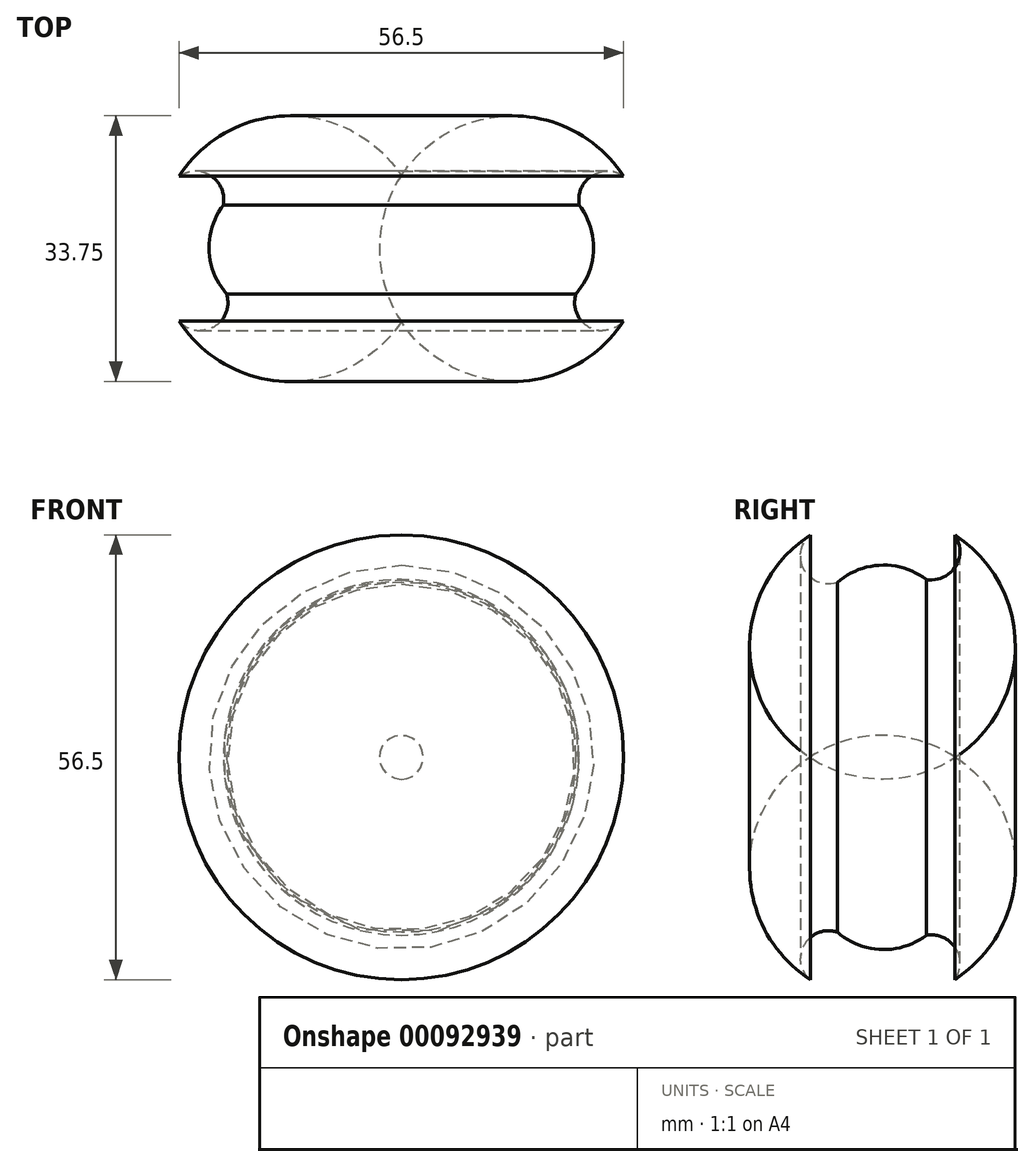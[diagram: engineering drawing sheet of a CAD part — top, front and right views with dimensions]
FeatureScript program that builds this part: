
annotation { "Feature Type Name" : "Feature", "Feature Type Description" : "" }
export const myFeature = defineFeature(function(context is Context, id is Id, definition is map)
    precondition{}
    {
        {
            var Q0;
            Q0=qCreatedBy(makeId("Top.planeOp"),FACE);
            var sketch = newSketch(context, id + "F0", { "sketchPlane" : qUnion([Q0])});
            skArc(sketch, "E0", {"start": v(22.2, -8.17) * mm, "mid": v(24.42, -2.6) * mm, "end": v(22.6, 3.13) * mm});
            skArc(sketch, "E1", {"start": v(28.25, -11.6) * mm, "mid": v(30.97, -2.42) * mm, "end": v(28.25, 6.76) * mm});
            skArc(sketch, "E2", {"start": v(28.25, 6.76) * mm, "mid": v(24.21, 6.83) * mm, "end": v(22.6, 3.13) * mm});
            skArc(sketch, "E3", {"start": v(22.2, -8.17) * mm, "mid": v(23.82, -12.37) * mm, "end": v(28.25, -11.6) * mm});
            skLineSegment(sketch, "E4", {"start": v(0, 12.2) * mm, "end": v(0, -15.03) * mm});
            skSolve(sketch);
        }
        {
            var Q0;
            Q0=makeQuery(id+"F0.imprint","IMPRINT",FACE,{"disambiguationData":[TD([[makeQuery(id+"F0.imprint","IMPRINT",EDGE,{"derivedFrom":sQuery(id+"F0.wireOp",EDGE,"E0")}),-1.0]])]});
            var Q1;
            Q1=sQuery(id+"F0.wireOp",EDGE,"E4");
            revolve(context, id + "F1", {"entities" : qUnion([Q0]), "axis" : qUnion([Q1]), "revolveType" : RevolveType.FULL});
        }
        {
            var Q0;
            Q0=qCreatedBy(makeId("Top.planeOp"),FACE);
            cPlane(context, id + "F2", {"entities" : qUnion([Q0]), "cplaneType" : CPlaneType.OFFSET, "offset" : 29 * mm, "width" : 152.4 * mm, "height" : 152.4 * mm});
        }
        {
            var Q0;
            Q0=qCreatedBy(id+"F2.planeOp",FACE);
            var sketch = newSketch(context, id + "F3", { "sketchPlane" : qUnion([Q0])});
            skCircle(sketch, "E5", {"center": v(0, -2.72) * mm, "radius": 23.46 * mm});
            skSolve(sketch);
        }
        {
            var Q0;
            Q0 = qSketchRegion(id + "F3", true);
            extrude(context, id + "F4", {"entities" : qUnion([Q0]), "operationType" : NewBodyOperationType.ADD, "depth" : 7 * mm});
        }
        {
            var Q0;
            Q0=makeQuery(id+"F4.opExtrude","CAP_FACE",FACE,{"disambiguationData":[OSD([sQuery(id+"F3.wireOp",EDGE,"E5")])],"isStart":false});
            var sketch = newSketch(context, id + "F5", { "sketchPlane" : qUnion([Q0])});
            skCircle(sketch, "E6", {"center": v(0, -2.72) * mm, "radius": 21.3 * mm});
            skSolve(sketch);
        }
        {
            var Q0;
            Q0 = qSketchRegion(id + "F5", true);
            extrude(context, id + "F6", {"entities" : qUnion([Q0]), "operationType" : NewBodyOperationType.REMOVE, "oppositeDirection" : true, "depth" : 2 * mm});
        }
        {
            var Q0;
            Q0=makeQuery(id+"F6.boolean.opBoolean","COPY",FACE,{"derivedFrom":makeQuery(id+"F6.opExtrude","CAP_FACE",FACE,{"disambiguationData":[OSD([sQuery(id+"F5.wireOp",EDGE,"E6")])],"isStart":false})});
            var sketch = newSketch(context, id + "F7", { "sketchPlane" : qUnion([Q0])});
            skLineSegment(sketch, "E7.bottom", {"start": v(-11.46, 11.21) * mm, "end": v(11.54, 11.21) * mm});
            skLineSegment(sketch, "E7.top", {"start": v(-11.46, 6.21) * mm, "end": v(-6.41, 6.21) * mm});
            skLineSegment(sketch, "E7.left", {"start": v(-11.46, 11.21) * mm, "end": v(-11.46, 6.21) * mm});
            skLineSegment(sketch, "E7.right", {"start": v(11.54, 11.21) * mm, "end": v(11.54, 6.21) * mm});
            skArc(sketch, "E8", {"start": v(-6.41, 6.21) * mm, "mid": v(-11, -2.84) * mm, "end": v(-6.22, -11.8) * mm});
            skLineSegment(sketch, "E9.bottom", {"start": v(11.54, -11.8) * mm, "end": v(6.22, -11.8) * mm});
            skLineSegment(sketch, "E9.top", {"start": v(11.54, -16.8) * mm, "end": v(-11.46, -16.8) * mm});
            skLineSegment(sketch, "E9.left", {"start": v(11.54, -11.8) * mm, "end": v(11.54, -16.8) * mm});
            skLineSegment(sketch, "E9.right", {"start": v(-11.46, -11.8) * mm, "end": v(-11.46, -16.8) * mm});
            skLineSegment(sketch, "E10.trimOffspring", {"start": v(6.41, 6.21) * mm, "end": v(11.54, 6.21) * mm});
            skLineSegment(sketch, "E11.trimOffspring", {"start": v(-6.22, -11.8) * mm, "end": v(-11.46, -11.8) * mm});
            skArc(sketch, "E12.trimOffspring", {"start": v(6.22, -11.8) * mm, "mid": v(11, -2.84) * mm, "end": v(6.41, 6.21) * mm});
            skSolve(sketch);
        }
        {
            var Q0;
            Q0 = qSketchRegion(id + "F7", true);
            extrude(context, id + "F8", {"entities" : qUnion([Q0]), "operationType" : NewBodyOperationType.ADD, "depth" : 3.5 * mm});
        }
        {
            var Q0;
            Q0=makeQuery(id+"F8.opExtrude","CAP_FACE",FACE,{"disambiguationData":[OSD([sQuery(id+"F7.wireOp",EDGE,"E7.bottom"),sQuery(id+"F7.wireOp",EDGE,"E7.top"),sQuery(id+"F7.wireOp",EDGE,"E7.left"),sQuery(id+"F7.wireOp",EDGE,"E7.right"),sQuery(id+"F7.wireOp",EDGE,"E8"),sQuery(id+"F7.wireOp",EDGE,"E9.bottom"),sQuery(id+"F7.wireOp",EDGE,"E9.top"),sQuery(id+"F7.wireOp",EDGE,"E9.left"),sQuery(id+"F7.wireOp",EDGE,"E9.right"),sQuery(id+"F7.wireOp",EDGE,"E10.trimOffspring"),sQuery(id+"F7.wireOp",EDGE,"E11.trimOffspring"),sQuery(id+"F7.wireOp",EDGE,"E12.trimOffspring")])],"isStart":false});
            var sketch = newSketch(context, id + "F9", { "sketchPlane" : qUnion([Q0])});
            skCircle(sketch, "E13", {"center": v(0, -2.72) * mm, "radius": 8.07 * mm});
            skSolve(sketch);
        }
        {
            var Q0;
            Q0 = qSketchRegion(id + "F9", true);
            extrude(context, id + "F10", {"entities" : qUnion([Q0]), "operationType" : NewBodyOperationType.REMOVE, "oppositeDirection" : true, "depth" : 2 * mm});
        }
        {
            var Q0;
            Q0=makeQuery(id+"F4.opExtrude","CAP_EDGE",EDGE,{"disambiguationData":[OSD([sQuery(id+"F3.wireOp",EDGE,"E5")])],"isStart":true});
            var Q1;
            Q1=makeQuery(id+"F4.opExtrude","CAP_EDGE",EDGE,{"disambiguationData":[OSD([sQuery(id+"F3.wireOp",EDGE,"E5")])],"isStart":false});
            fillet(context, id + "F11", {"entities" : qUnion([Q0, Q1]), "radius" : 2 * mm, "tangentPropagation" : true, "allowEdgeOverflow" : false});
        }
        {
            var Q0;
            Q0=makeQuery(id+"F11.opFillet","BLEND_EDGE",EDGE,{"blendedFrom":[makeQuery(id+"F4.opExtrude","CAP_EDGE",EDGE,{"disambiguationData":[OSD([sQuery(id+"F3.wireOp",EDGE,"E5")])],"isStart":false}),makeQuery(id+"F6.boolean.opBoolean","COPY",FACE,{"derivedFrom":makeQuery(id+"F6.opExtrude","SWEPT_FACE",FACE,{"disambiguationData":[OSD([sQuery(id+"F5.wireOp",EDGE,"E6")])]})})],"blendedInto":[makeQuery(id+"F6.boolean.opBoolean","COPY",FACE,{"derivedFrom":makeQuery(id+"F6.opExtrude","SWEPT_FACE",FACE,{"disambiguationData":[OSD([sQuery(id+"F5.wireOp",EDGE,"E6")])]})})]});
            var Q1;
            Q1=makeQuery(id+"F8.opExtrude","CAP_EDGE",EDGE,{"disambiguationData":[OSD([sQuery(id+"F7.wireOp",EDGE,"E9.top")])],"isStart":false});
            var Q2;
            Q2=makeQuery(id+"F8.opExtrude","CAP_EDGE",EDGE,{"disambiguationData":[OSD([sQuery(id+"F7.wireOp",EDGE,"E9.left")])],"isStart":false});
            var Q3;
            Q3=makeQuery(id+"F8.opExtrude","CAP_EDGE",EDGE,{"disambiguationData":[OSD([sQuery(id+"F7.wireOp",EDGE,"E9.bottom")])],"isStart":false});
            var Q4;
            Q4=makeQuery(id+"F8.opExtrude","CAP_EDGE",EDGE,{"disambiguationData":[OSD([sQuery(id+"F7.wireOp",EDGE,"E12.trimOffspring")])],"isStart":false});
            var Q5;
            Q5=makeQuery(id+"F8.opExtrude","CAP_EDGE",EDGE,{"disambiguationData":[OSD([sQuery(id+"F7.wireOp",EDGE,"E10.trimOffspring")])],"isStart":false});
            var Q6;
            Q6=makeQuery(id+"F8.opExtrude","CAP_EDGE",EDGE,{"disambiguationData":[OSD([sQuery(id+"F7.wireOp",EDGE,"E7.right")])],"isStart":false});
            var Q7;
            Q7=makeQuery(id+"F8.opExtrude","CAP_EDGE",EDGE,{"disambiguationData":[OSD([sQuery(id+"F7.wireOp",EDGE,"E7.bottom")])],"isStart":false});
            var Q8;
            Q8=makeQuery(id+"F8.opExtrude","CAP_EDGE",EDGE,{"disambiguationData":[OSD([sQuery(id+"F7.wireOp",EDGE,"E7.left")])],"isStart":false});
            var Q9;
            Q9=makeQuery(id+"F8.opExtrude","CAP_EDGE",EDGE,{"disambiguationData":[OSD([sQuery(id+"F7.wireOp",EDGE,"E7.top")])],"isStart":false});
            var Q10;
            Q10=makeQuery(id+"F8.opExtrude","CAP_EDGE",EDGE,{"disambiguationData":[OSD([sQuery(id+"F7.wireOp",EDGE,"E8")])],"isStart":false});
            var Q11;
            Q11=makeQuery(id+"F8.opExtrude","CAP_EDGE",EDGE,{"disambiguationData":[OSD([sQuery(id+"F7.wireOp",EDGE,"E11.trimOffspring")])],"isStart":false});
            var Q12;
            Q12=makeQuery(id+"F10.boolean.opBoolean","COPY",EDGE,{"derivedFrom":makeQuery(id+"F10.opExtrude","CAP_EDGE",EDGE,{"disambiguationData":[OSD([sQuery(id+"F9.wireOp",EDGE,"E13")])],"isStart":true})});
            var Q13;
            Q13=makeQuery(id+"F8.opExtrude","CAP_EDGE",EDGE,{"disambiguationData":[OSD([sQuery(id+"F7.wireOp",EDGE,"E9.right")])],"isStart":false});
            var Q14;
            Q14=makeQuery(id+"F8.opExtrude","SWEPT_EDGE",EDGE,{"disambiguationData":[OSD([sQuery(id+"F7.wireOp",EDGE,"E9.top"),sQuery(id+"F7.wireOp",EDGE,"E9.right")])]});
            var Q15;
            Q15=makeQuery(id+"F8.opExtrude","SWEPT_EDGE",EDGE,{"disambiguationData":[OSD([sQuery(id+"F7.wireOp",EDGE,"E9.right"),sQuery(id+"F7.wireOp",EDGE,"E11.trimOffspring")])]});
            var Q16;
            Q16=makeQuery(id+"F8.opExtrude","SWEPT_EDGE",EDGE,{"disambiguationData":[OSD([sQuery(id+"F7.wireOp",EDGE,"E7.top"),sQuery(id+"F7.wireOp",EDGE,"E7.left")])]});
            var Q17;
            Q17=makeQuery(id+"F8.opExtrude","SWEPT_EDGE",EDGE,{"disambiguationData":[OSD([sQuery(id+"F7.wireOp",EDGE,"E7.bottom"),sQuery(id+"F7.wireOp",EDGE,"E7.left")])]});
            var Q18;
            Q18=makeQuery(id+"F8.opExtrude","SWEPT_EDGE",EDGE,{"disambiguationData":[OSD([sQuery(id+"F7.wireOp",EDGE,"E7.bottom"),sQuery(id+"F7.wireOp",EDGE,"E7.right")])]});
            var Q19;
            Q19=makeQuery(id+"F8.opExtrude","SWEPT_EDGE",EDGE,{"disambiguationData":[OSD([sQuery(id+"F7.wireOp",EDGE,"E7.right"),sQuery(id+"F7.wireOp",EDGE,"E10.trimOffspring")])]});
            var Q20;
            Q20=makeQuery(id+"F8.opExtrude","SWEPT_EDGE",EDGE,{"disambiguationData":[OSD([sQuery(id+"F7.wireOp",EDGE,"E9.top"),sQuery(id+"F7.wireOp",EDGE,"E9.left")])]});
            var Q21;
            Q21=makeQuery(id+"F8.opExtrude","SWEPT_EDGE",EDGE,{"disambiguationData":[OSD([sQuery(id+"F7.wireOp",EDGE,"E9.bottom"),sQuery(id+"F7.wireOp",EDGE,"E9.left")])]});
            fillet(context, id + "F12", {"entities" : qUnion([Q0, Q1, Q2, Q3, Q4, Q5, Q6, Q7, Q8, Q9, Q10, Q11, Q12, Q13, Q14, Q15, Q16, Q17, Q18, Q19, Q20, Q21]), "radius" : 0.4 * mm, "tangentPropagation" : true, "allowEdgeOverflow" : false});
        }
    });
